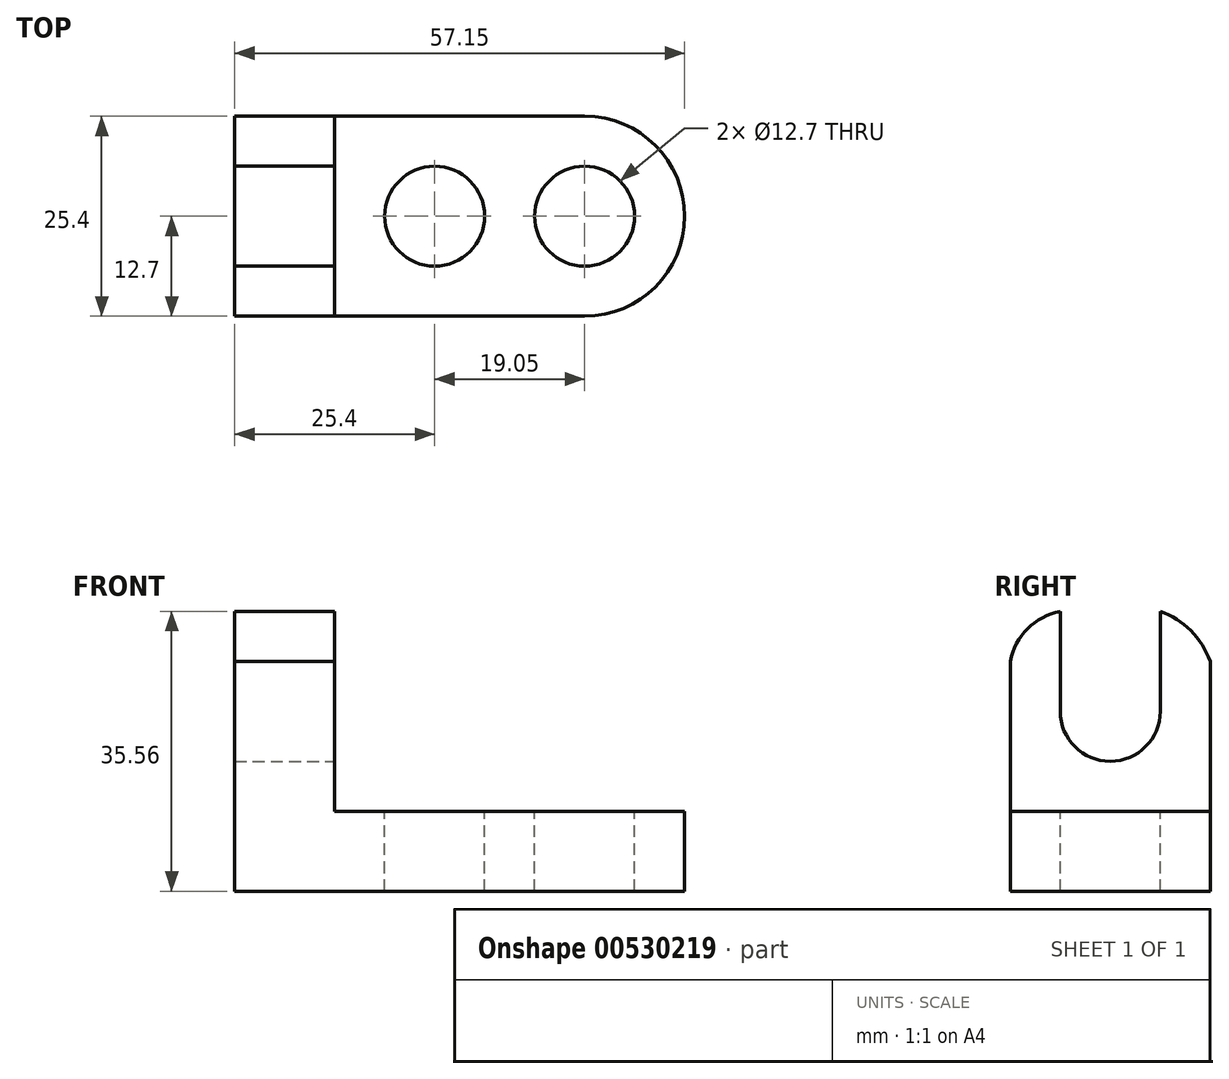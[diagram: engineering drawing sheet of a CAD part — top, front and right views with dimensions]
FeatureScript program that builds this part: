
annotation { "Feature Type Name" : "Feature", "Feature Type Description" : "" }
export const myFeature = defineFeature(function(context is Context, id is Id, definition is map)
    precondition{}
    {
        {
            var Q0;
            Q0=qCreatedBy(makeId("Front.planeOp"),FACE);
            var sketch = newSketch(context, id + "F0", { "sketchPlane" : qUnion([Q0])});
            skLineSegment(sketch, "E0", {"start": v(0, 0) * mm, "end": v(-44.45, 0) * mm});
            skLineSegment(sketch, "E1", {"start": v(-44.45, 0) * mm, "end": v(-44.45, 10.16) * mm});
            skLineSegment(sketch, "E2", {"start": v(-44.45, 10.16) * mm, "end": v(0, 10.16) * mm});
            skLineSegment(sketch, "E3", {"start": v(0, 10.16) * mm, "end": v(0, 0) * mm});
            skSolve(sketch);
        }
        {
            var Q0;
            Q0 = qSketchRegion(id + "F0", true);
            extrude(context, id + "F1", {"entities" : qUnion([Q0]), "depth" : 25.4 * mm, "offsetDistance" : 25.4 * mm});
        }
        {
            var Q0;
            Q0=makeQuery(id+"F1.opExtrude","SWEPT_FACE",FACE,{"disambiguationData":[OSD([sQuery(id+"F0.wireOp",EDGE,"E2")])]});
            var sketch = newSketch(context, id + "F2", { "sketchPlane" : qUnion([Q0])});
            skArc(sketch, "E4", {"start": v(0, -25.4) * mm, "mid": v(12.7, -12.7) * mm, "end": v(0, 0) * mm});
            skSolve(sketch);
        }
        {
            var Q0;
            Q0 = qSketchRegion(id + "F2", true);
            var Q1;
            Q1=makeQuery(id+"F2.imprint","IMPRINT",FACE,{"disambiguationData":[TD([[makeQuery(id+"F2.imprint","IMPRINT",EDGE,{"derivedFrom":sQuery(id+"F2.wireOp",EDGE,"E4")}),1.0]])]});
            extrude(context, id + "F3", {"entities" : qUnion([Q0, Q1]), "operationType" : NewBodyOperationType.ADD, "oppositeDirection" : true, "depth" : 10.16 * mm, "offsetDistance" : 25.4 * mm});
        }
        {
            var Q0;
            {var subQ0=sQuery(id+"F0.wireOp",EDGE,"E2");Q0=makeQuery(id+"F3.boolean.opBoolean","MERGE",FACE,{"derivedFrom":[makeQuery(id+"F1.opExtrude","SWEPT_FACE",FACE,{"disambiguationData":[OSD([subQ0])]}),makeQuery(id+"F3.opExtrude","CAP_FACE",FACE,{"disambiguationData":[OSD([subQ0,sQuery(id+"F0.wireOp",EDGE,"E3"),sQuery(id+"F2.wireOp",EDGE,"E4")])],"isStart":true})]});}
            var sketch = newSketch(context, id + "F4", { "sketchPlane" : qUnion([Q0])});
            skLineSegment(sketch, "E5", {"start": v(-31.75, 0) * mm, "end": v(-31.75, -25.4) * mm});
            skLineSegment(sketch, "E6", {"start": v(-31.75, -25.4) * mm, "end": v(-44.45, -25.4) * mm});
            skLineSegment(sketch, "E7", {"start": v(-44.45, -25.4) * mm, "end": v(-44.45, 0) * mm});
            skLineSegment(sketch, "E8", {"start": v(-44.45, 0) * mm, "end": v(-31.75, 0) * mm});
            skSolve(sketch);
        }
        {
            var Q0;
            Q0 = qSketchRegion(id + "F4", true);
            extrude(context, id + "F5", {"entities" : qUnion([Q0]), "operationType" : NewBodyOperationType.ADD, "depth" : 19.05 * mm, "offsetDistance" : 25.4 * mm});
        }
        {
            var Q0;
            Q0=makeQuery(id+"F5.opExtrude","CAP_FACE",FACE,{"disambiguationData":[OSD([sQuery(id+"F4.wireOp",EDGE,"E5"),sQuery(id+"F4.wireOp",EDGE,"E6"),sQuery(id+"F4.wireOp",EDGE,"E7"),sQuery(id+"F4.wireOp",EDGE,"E8")])],"isStart":false});
            extrude(context, id + "F6", {"entities" : qUnion([Q0]), "operationType" : NewBodyOperationType.ADD, "depth" : 6.35 * mm, "offsetDistance" : 25.4 * mm});
        }
        {
            var Q0;
            {var subQ0=sQuery(id+"F4.wireOp",EDGE,"E5");Q0=makeQuery(id+"F6.boolean.opBoolean","MERGE",FACE,{"derivedFrom":[makeQuery(id+"F5.opExtrude","SWEPT_FACE",FACE,{"disambiguationData":[OSD([subQ0])]}),makeQuery(id+"F6.opExtrude","SWEPT_FACE",FACE,{"disambiguationData":[OSD([subQ0])]})]});}
            var sketch = newSketch(context, id + "F7", { "sketchPlane" : qUnion([Q0])});
            skArc(sketch, "E9", {"start": v(-19.05, 35.56) * mm, "mid": v(-23.18, 33.34) * mm, "end": v(-25.4, 29.21) * mm});
            skSolve(sketch);
        }
        {
            var Q0;
            {var subQ5=sQuery(id+"F7.wireOp",EDGE,"E9");Q0=makeQuery(id+"F7.imprint","IMPRINT",FACE,{"disambiguationData":[TD([[makeQuery(id+"F7.imprint","IMPRINT",EDGE,{"derivedFrom":subQ5}),1.0]])]});}
            var sketch = newSketch(context, id + "F8", { "sketchPlane" : qUnion([Q0])});
            skArc(sketch, "E10", {"start": v(0, 29.21) * mm, "mid": v(-2.46, 33.1) * mm, "end": v(-6.35, 35.56) * mm});
            skSolve(sketch);
        }
        {
            var Q0;
            {var subQ0=sQuery(id+"F7.wireOp",EDGE,"E9");Q0=makeQuery(id+"F7.imprint","IMPRINT",FACE,{"disambiguationData":[TD([[makeQuery(id+"F7.imprint","IMPRINT",EDGE,{"derivedFrom":subQ0}),-1.0]])]});}
            extrude(context, id + "F9", {"entities" : qUnion([Q0]), "operationType" : NewBodyOperationType.REMOVE, "oppositeDirection" : true, "depth" : 25.4 * mm, "offsetDistance" : 25.4 * mm});
        }
        {
            var Q0;
            {var subQ0=sQuery(id+"F8.wireOp",EDGE,"E10");Q0=makeQuery(id+"F8.imprint","IMPRINT",FACE,{"disambiguationData":[TD([[makeQuery(id+"F8.imprint","IMPRINT",EDGE,{"derivedFrom":subQ0}),-1.0]])]});}
            extrude(context, id + "F10", {"entities" : qUnion([Q0]), "operationType" : NewBodyOperationType.ADD, "depth" : 25.4 * mm, "offsetDistance" : 25.4 * mm});
        }
        {
            var Q0;
            Q0=makeQuery(id+"F10.opExtrude","CAP_FACE",FACE,{"disambiguationData":[OSD([sQuery(id+"F0.wireOp",EDGE,"E2"),sQuery(id+"F4.wireOp",EDGE,"E5"),sQuery(id+"F4.wireOp",EDGE,"E8"),sQuery(id+"F8.wireOp",EDGE,"E10")])],"isStart":false});
            extrude(context, id + "F11", {"entities" : qUnion([Q0]), "operationType" : NewBodyOperationType.REMOVE, "oppositeDirection" : true, "depth" : 50.8 * mm, "offsetDistance" : 25.4 * mm});
        }
        {
            var Q0;
            {var subQ0=sQuery(id+"F4.wireOp",EDGE,"E5");Q0=makeQuery(id+"F6.boolean.opBoolean","MERGE",FACE,{"derivedFrom":[makeQuery(id+"F5.opExtrude","SWEPT_FACE",FACE,{"disambiguationData":[OSD([subQ0])]}),makeQuery(id+"F6.opExtrude","SWEPT_FACE",FACE,{"disambiguationData":[OSD([subQ0])]})]});}
            var sketch = newSketch(context, id + "F12", { "sketchPlane" : qUnion([Q0])});
            skLineSegment(sketch, "E11", {"start": v(-19.05, 35.56) * mm, "end": v(-19.05, 22.86) * mm});
            skLineSegment(sketch, "E12", {"start": v(-19.05, 22.86) * mm, "end": v(-6.35, 22.86) * mm});
            skLineSegment(sketch, "E13", {"start": v(-6.35, 22.86) * mm, "end": v(-6.35, 35.56) * mm});
            skLineSegment(sketch, "E14", {"start": v(-6.35, 35.56) * mm, "end": v(-19.05, 35.56) * mm});
            skArc(sketch, "E15", {"start": v(-19.05, 22.86) * mm, "mid": v(-12.7, 16.51) * mm, "end": v(-6.35, 22.86) * mm});
            skSolve(sketch);
        }
        {
            var Q0;
            Q0 = qSketchRegion(id + "F12", true);
            extrude(context, id + "F13", {"entities" : qUnion([Q0]), "operationType" : NewBodyOperationType.REMOVE, "oppositeDirection" : true, "depth" : 25.4 * mm, "offsetDistance" : 25.4 * mm});
        }
        {
            var Q0;
            {var subQ0=sQuery(id+"F0.wireOp",EDGE,"E2");Q0=makeQuery(id+"F3.boolean.opBoolean","MERGE",FACE,{"derivedFrom":[makeQuery(id+"F1.opExtrude","SWEPT_FACE",FACE,{"disambiguationData":[OSD([subQ0])]}),makeQuery(id+"F3.opExtrude","CAP_FACE",FACE,{"disambiguationData":[OSD([subQ0,sQuery(id+"F0.wireOp",EDGE,"E3"),sQuery(id+"F2.wireOp",EDGE,"E4")])],"isStart":true})]});}
            var sketch = newSketch(context, id + "F14", { "sketchPlane" : qUnion([Q0])});
            skCircle(sketch, "E16", {"center": v(-19.05, -12.7) * mm, "radius": 6.35 * mm});
            skPoint(sketch, "E16.centerSnap0", {"position": v(-31.75, -12.7) * mm});
            skSolve(sketch);
        }
        {
            var Q0;
            Q0=makeQuery(id+"F14.imprint","IMPRINT",FACE,{"disambiguationData":[TD([[makeQuery(id+"F14.imprint","IMPRINT",EDGE,{"derivedFrom":sQuery(id+"F14.wireOp",EDGE,"E16")}),1.0]])]});
            extrude(context, id + "F15", {"entities" : qUnion([Q0]), "operationType" : NewBodyOperationType.REMOVE, "oppositeDirection" : true, "depth" : 25.4 * mm, "offsetDistance" : 25.4 * mm});
        }
        {
            var Q0;
            {var subQ0=sQuery(id+"F0.wireOp",EDGE,"E2");Q0=makeQuery(id+"F3.boolean.opBoolean","MERGE",FACE,{"derivedFrom":[makeQuery(id+"F1.opExtrude","SWEPT_FACE",FACE,{"disambiguationData":[OSD([subQ0])]}),makeQuery(id+"F3.opExtrude","CAP_FACE",FACE,{"disambiguationData":[OSD([subQ0,sQuery(id+"F0.wireOp",EDGE,"E3"),sQuery(id+"F2.wireOp",EDGE,"E4")])],"isStart":true})]});}
            var sketch = newSketch(context, id + "F16", { "sketchPlane" : qUnion([Q0])});
            skCircle(sketch, "E17", {"center": v(0, -12.7) * mm, "radius": 6.35 * mm});
            skSolve(sketch);
        }
        {
            var Q0;
            Q0=makeQuery(id+"F16.imprint","IMPRINT",FACE,{"disambiguationData":[TD([[makeQuery(id+"F16.imprint","IMPRINT",EDGE,{"derivedFrom":sQuery(id+"F16.wireOp",EDGE,"E17")}),1.0]])]});
            extrude(context, id + "F17", {"entities" : qUnion([Q0]), "operationType" : NewBodyOperationType.REMOVE, "oppositeDirection" : true, "depth" : 25.4 * mm, "offsetDistance" : 25.4 * mm});
        }
    });
